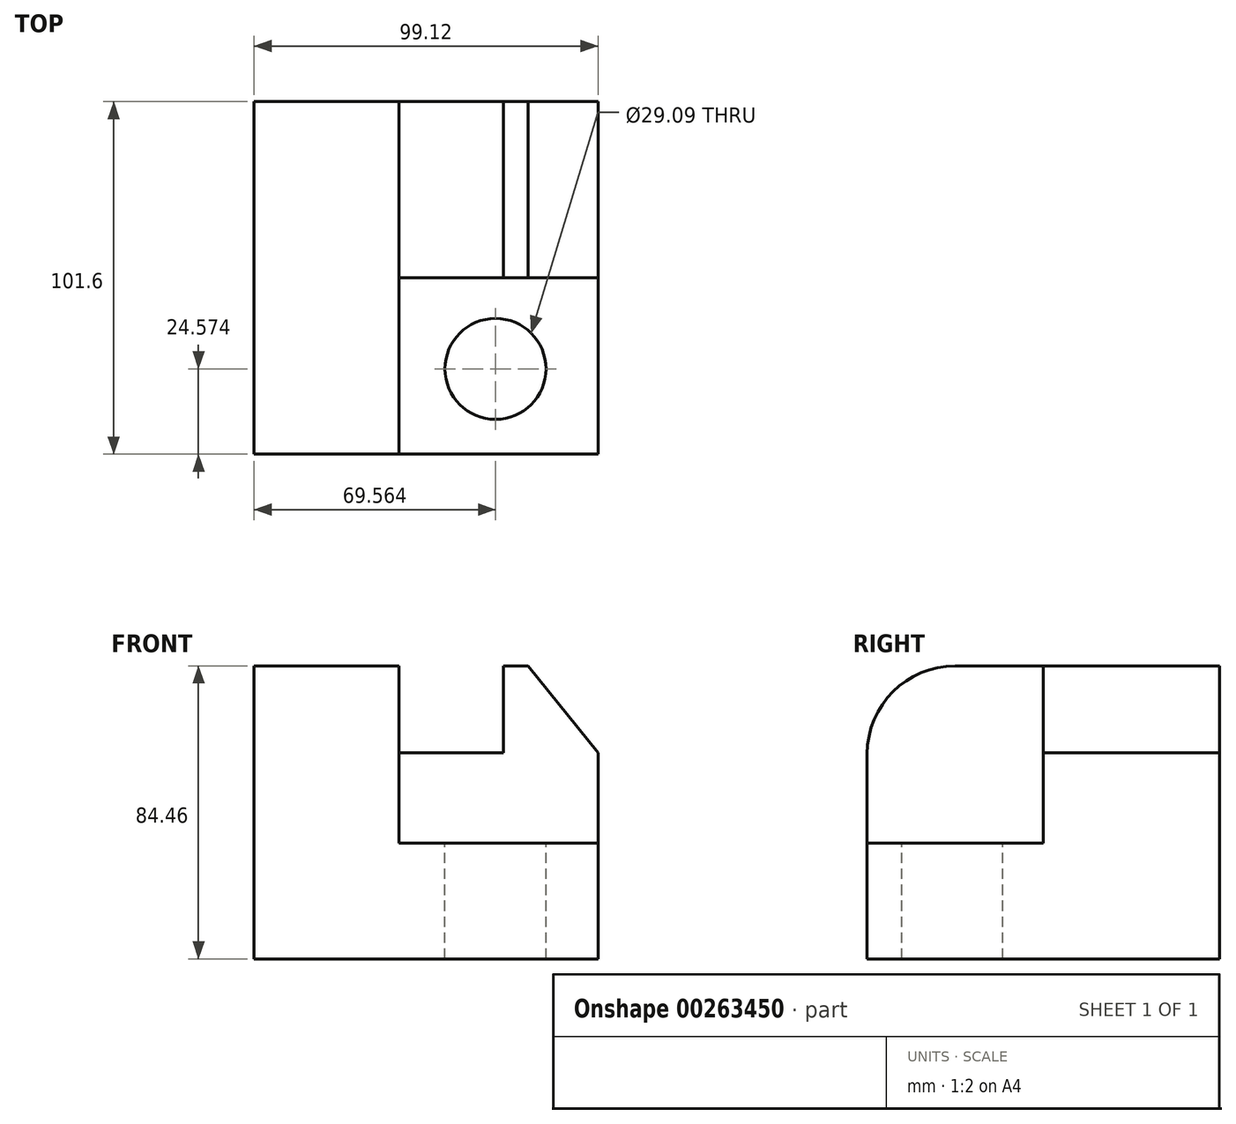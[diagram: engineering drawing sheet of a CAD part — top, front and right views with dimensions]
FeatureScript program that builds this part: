
annotation { "Feature Type Name" : "Feature", "Feature Type Description" : "" }
export const myFeature = defineFeature(function(context is Context, id is Id, definition is map)
    precondition{}
    {
        {
            var Q0;
            Q0=qCreatedBy(makeId("Front.planeOp"),FACE);
            var sketch = newSketch(context, id + "F0", { "sketchPlane" : qUnion([Q0])});
            skLineSegment(sketch, "E0", {"start": v(-48.45, -33.34) * mm, "end": v(50.67, -33.34) * mm});
            skLineSegment(sketch, "E1", {"start": v(50.67, -33.34) * mm, "end": v(50.67, 26) * mm});
            skLineSegment(sketch, "E2", {"start": v(50.67, 26) * mm, "end": v(30.45, 51.12) * mm});
            skLineSegment(sketch, "E3", {"start": v(30.45, 51.12) * mm, "end": v(23.34, 51.12) * mm});
            skLineSegment(sketch, "E4", {"start": v(23.34, 51.12) * mm, "end": v(23.34, 26) * mm});
            skLineSegment(sketch, "E5", {"start": v(23.34, 26) * mm, "end": v(-6.67, 26) * mm});
            skLineSegment(sketch, "E6", {"start": v(-6.67, 26) * mm, "end": v(-6.67, 51.12) * mm});
            skLineSegment(sketch, "E7", {"start": v(-6.67, 51.12) * mm, "end": v(-48.45, 51.12) * mm});
            skLineSegment(sketch, "E8", {"start": v(-48.45, 51.12) * mm, "end": v(-48.45, -33.34) * mm});
            skSolve(sketch);
        }
        {
            var Q0;
            Q0 = qSketchRegion(id + "F0", true);
            extrude(context, id + "F1", {"entities" : qUnion([Q0]), "endBound" : BoundingType.SYMMETRIC, "depth" : 101.6 * mm});
        }
        {
            var Q0;
            Q0=makeQuery(id+"F1.opExtrude","CAP_FACE",FACE,{"disambiguationData":[OSD([sQuery(id+"F0.wireOp",EDGE,"E0"),sQuery(id+"F0.wireOp",EDGE,"E1"),sQuery(id+"F0.wireOp",EDGE,"E2"),sQuery(id+"F0.wireOp",EDGE,"E3"),sQuery(id+"F0.wireOp",EDGE,"E4"),sQuery(id+"F0.wireOp",EDGE,"E5"),sQuery(id+"F0.wireOp",EDGE,"E6"),sQuery(id+"F0.wireOp",EDGE,"E7"),sQuery(id+"F0.wireOp",EDGE,"E8")])],"isStart":false});
            var sketch = newSketch(context, id + "F2", { "sketchPlane" : qUnion([Q0])});
            skLineSegment(sketch, "E9", {"start": v(-6.67, 26) * mm, "end": v(-6.67, 0) * mm});
            skLineSegment(sketch, "E10", {"start": v(-6.67, 0) * mm, "end": v(50.67, 0) * mm});
            skSolve(sketch);
        }
        {
            var Q0;
            Q0=makeQuery(id+"F2.imprint","IMPRINT",FACE,{"disambiguationData":[TD([[makeQuery(id+"F2.imprint","IMPRINT",EDGE,{"derivedFrom":sQuery(id+"F2.wireOp",EDGE,"E9")}),1.0]])]});
            extrude(context, id + "F3", {"entities" : qUnion([Q0]), "operationType" : NewBodyOperationType.REMOVE, "oppositeDirection" : true, "depth" : 50.8 * mm});
        }
        {
            var Q0;
            Q0=makeQuery(id+"F1.opExtrude","CAP_EDGE",EDGE,{"disambiguationData":[OSD([sQuery(id+"F0.wireOp",EDGE,"E7")])],"isStart":false});
            fillet(context, id + "F4", {"entities" : qUnion([Q0]), "radius" : 25.4 * mm, "tangentPropagation" : true, "allowEdgeOverflow" : false});
        }
        {
            var Q0;
            Q0=qCreatedBy(makeId("Top.planeOp"),FACE);
            var sketch = newSketch(context, id + "F5", { "sketchPlane" : qUnion([Q0])});
            skCircle(sketch, "E11", {"center": v(21.11, -26.23) * mm, "radius": 14.54 * mm});
            skSolve(sketch);
        }
        {
            var Q0;
            Q0 = qSketchRegion(id + "F5", true);
            extrude(context, id + "F6", {"entities" : qUnion([Q0]), "operationType" : NewBodyOperationType.REMOVE, "endBound" : BoundingType.THROUGH_ALL, "oppositeDirection" : true, "depth" : 25.4 * mm});
        }
    });
